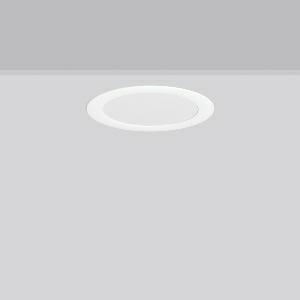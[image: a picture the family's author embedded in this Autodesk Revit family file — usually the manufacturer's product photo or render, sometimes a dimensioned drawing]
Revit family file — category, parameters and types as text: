
# Revit family: toledo_flat_round_e_672224_002_1_04_5b04
name_source: partatom
category: Lighting Fixtures
units: mm (PartAtom-declared; Revit-internal decimal feet)

## family parameters
Cut with Voids When Loaded = No
Host = Face
Light Source = No
Part Type = Normal
Room Calculation Point = No
Round Connector Dimension = Use Diameter
Shared = No

## types (1)
- TOLEDO FLAT round E (1 x LED Modul 840, 1800 lm, 4000)
    Apparent Load = 17 VA
    CIE Flux Codes = 48 79 96 100 100
    Color Rendering = 80
    Color Temperature = 4000
    Default Elevation = 1800 mm  [stored 5.90551 ft]
    Description = Series: TOLEDO FLAT round
Ultra thin recessed downlight. For escape route illumination. Housing: die-cast aluminium, powder-coated. Lightguide and diffuser made of non-yellowing plastic (PMMA). Diffuser opal matt plastic. Ceiling installation with spring system. Including separate LED converter with connecting cable 250 mm. Self-contained system with automatic self-test and feedback to the RZB monitoring system MULTIDIGIT. External driver with simple plug-in locking system. 
Colour: white
Diameter: 255 mm
Height: 3 mm
Cut-out diameter: 234 mm
Recess height: 100 mm
Luminaire: recess height: 60-80 mm
Weight: 1.77 kg
Operating mode: maintained power mode
Duration time: 3 h
Lamp: LED
Socket: without socket
Colour temperature: 4000K
Colour rendering index (CRI): 80
System power: 17 W
Rated luminous flux: 1800 lm
Luminous flux, emergency: 460 lm
System power, emergency: -
Control gear: Regulated power supply
Protection class: I
Type of protection: IP 54
    Height = 0 mm  [stored 0 ft]
    Lamp = 1 x LED Modul 840
    Lamp Light Flux = 1800 lm
    Lamp count = 1
    Length = 255 mm
    Lifetime = 50000 h
    Luminous efficacy = 106 lm/W
    Manufacturer = RZB
    ModVariant = No
    Model = 672224.002.1.04
    Mounting Place = Ceiling
    Mounting Type = Recessed
    Number of Poles = 1
    OnlyDefault = Yes
    Power Factor = 1
    Product Name = TOLEDO FLAT round E
    Product group = Recessed downlights
    ProductGroupID = 402
    Protection Class = Protection class I
    Protection Degree = IP 40
    RLX_Detail_Level = 1
    RLX_Emergency_Light_Flux = 460 lm
    RLX_Emergency_Type = 3
    RLX_Emergency_Type_DB = Yes
    RlxData = <blob elided: 30605 chars, md5=8ab3108e>
    Socket = socket
    Standby Power = 0 W
    System Light Flux = 1800 lm
    System Power = 17 W
    Type Comments = Product without accessories
    Type Image = 901453.002.jpg
    URL = http://relux.com
    VarID = ---
    Voltage = 0 V
    Weight = 0.00 kg
    Width = 0 mm  [stored 0 ft]

note: [stored X ft] marks values corroborated as IEEE doubles in the binary element streams (Revit-internal decimal feet)

## geometry (parser evidence)
native form markers: Blend x4, Sweep x14
no freeform markers — native parametric forms only
